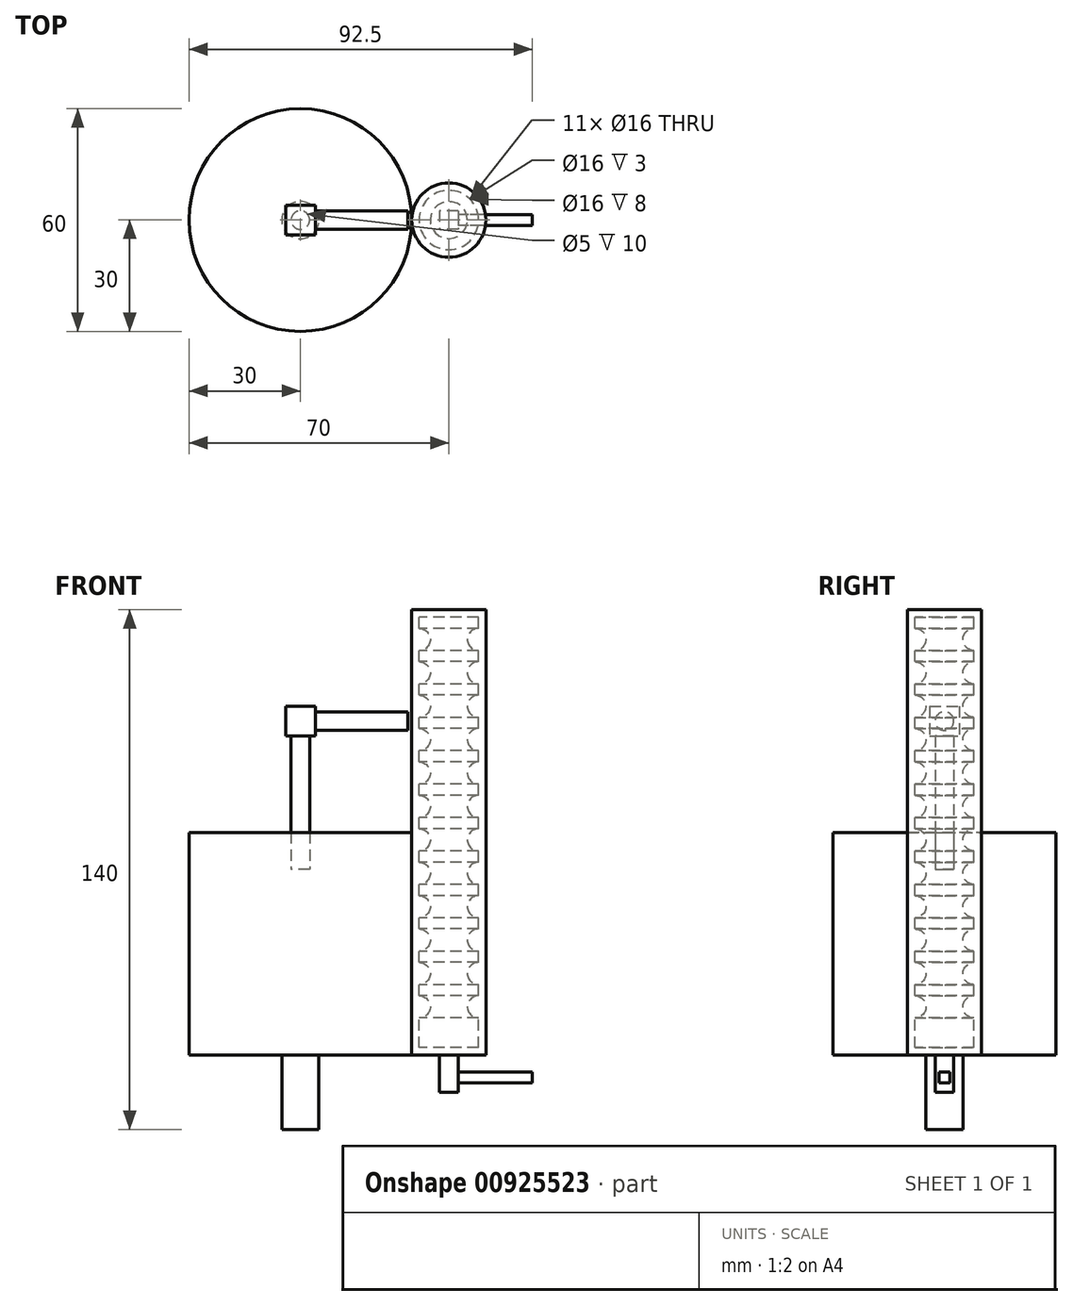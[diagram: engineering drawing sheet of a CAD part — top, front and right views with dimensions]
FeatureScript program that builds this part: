
annotation { "Feature Type Name" : "Feature", "Feature Type Description" : "" }
export const myFeature = defineFeature(function(context is Context, id is Id, definition is map)
    precondition{}
    {
        {
            var Q0;
            Q0=qCreatedBy(makeId("Top.planeOp"),FACE);
            var sketch = newSketch(context, id + "F0", { "sketchPlane" : qUnion([Q0])});
            skCircle(sketch, "E0", {"center": v(0, 0) * mm, "radius": 30 * mm});
            skSolve(sketch);
        }
        {
            var Q0;
            Q0=makeQuery(id+"F0.imprint","IMPRINT",FACE,{"disambiguationData":[TD([[makeQuery(id+"F0.imprint","IMPRINT",EDGE,{"derivedFrom":sQuery(id+"F0.wireOp",EDGE,"E0")}),1.0]])]});
            extrude(context, id + "F1", {"entities" : qUnion([Q0]), "depth" : 60 * mm, "offsetDistance" : 25 * mm});
        }
        {
            var Q0;
            Q0=qCreatedBy(makeId("Front.planeOp"),FACE);
            var sketch = newSketch(context, id + "F2", { "sketchPlane" : qUnion([Q0])});
            skLineSegment(sketch, "E1", {"start": v(40, 0) * mm, "end": v(40, 120) * mm, "construction": true});
            skLineSegment(sketch, "E2", {"start": v(40, 0) * mm, "end": v(40, 120) * mm});
            skLineSegment(sketch, "E3", {"start": v(50, 0) * mm, "end": v(50, 120) * mm});
            skLineSegment(sketch, "E4", {"start": v(50, 120) * mm, "end": v(40, 120) * mm});
            skLineSegment(sketch, "E5", {"start": v(40, 0) * mm, "end": v(50, 0) * mm});
            skSolve(sketch);
        }
        {
            var Q0;
            Q0 = qSketchRegion(id + "F2", true);
            var Q1;
            Q1=sQuery(id+"F2.wireOp",EDGE,"E2");
            revolve(context, id + "F3", {"surfaceOperationType" : NewSurfaceOperationType.NEW, "entities" : qUnion([Q0]), "axis" : qUnion([Q1]), "revolveType" : RevolveType.FULL});
        }
        {
            var Q0;
            Q0=qCreatedBy(makeId("Front.planeOp"),FACE);
            var sketch = newSketch(context, id + "F4", { "sketchPlane" : qUnion([Q0])});
            skLineSegment(sketch, "E6.bottom", {"start": v(40, 2) * mm, "end": v(48, 2) * mm});
            skLineSegment(sketch, "E6.top", {"start": v(40, 118) * mm, "end": v(48, 118) * mm});
            skLineSegment(sketch, "E6.left", {"start": v(40, 2) * mm, "end": v(40, 118) * mm});
            skLineSegment(sketch, "E6.right", {"start": v(48, 2) * mm, "end": v(48, 10) * mm});
            skArc(sketch, "E7", {"start": v(48, 115) * mm, "mid": v(45, 112) * mm, "end": v(48, 109) * mm});
            skArc(sketch, "E8.1.0.0", {"start": v(48, 106) * mm, "mid": v(45, 103) * mm, "end": v(48, 100) * mm});
            skArc(sketch, "E8.2.0.0", {"start": v(48, 97) * mm, "mid": v(45, 94) * mm, "end": v(48, 91) * mm});
            skLineSegment(sketch, "E8.direction1", {"start": v(48, 109) * mm, "end": v(48, 106) * mm, "construction": true});
            skArc(sketch, "E9.0.3.0", {"start": v(48, 88) * mm, "mid": v(45, 85) * mm, "end": v(48, 82) * mm});
            skArc(sketch, "E9.0.4.0", {"start": v(48, 79) * mm, "mid": v(45, 76) * mm, "end": v(48, 73) * mm});
            skArc(sketch, "E9.0.5.0", {"start": v(48, 70) * mm, "mid": v(45, 67) * mm, "end": v(48, 64) * mm});
            skArc(sketch, "E9.0.6.0", {"start": v(48, 61) * mm, "mid": v(45, 58) * mm, "end": v(48, 55) * mm});
            skArc(sketch, "E9.0.7.0", {"start": v(48, 52) * mm, "mid": v(45, 49) * mm, "end": v(48, 46) * mm});
            skArc(sketch, "E9.0.8.0", {"start": v(48, 43) * mm, "mid": v(45, 40) * mm, "end": v(48, 37) * mm});
            skArc(sketch, "E9.0.9.0", {"start": v(48, 34) * mm, "mid": v(45, 31) * mm, "end": v(48, 28) * mm});
            skArc(sketch, "E9.0.10.0", {"start": v(48, 25) * mm, "mid": v(45, 22) * mm, "end": v(48, 19) * mm});
            skArc(sketch, "E9.0.11.0", {"start": v(48, 16) * mm, "mid": v(45, 13) * mm, "end": v(48, 10) * mm});
            skLineSegment(sketch, "E10.trimOffspring", {"start": v(48, 115) * mm, "end": v(48, 118) * mm});
            skLineSegment(sketch, "E11.trimOffspring", {"start": v(48, 106) * mm, "end": v(48, 109) * mm});
            skLineSegment(sketch, "E12.trimOffspring", {"start": v(48, 97) * mm, "end": v(48, 100) * mm});
            skLineSegment(sketch, "E13.trimOffspring", {"start": v(48, 88) * mm, "end": v(48, 91) * mm});
            skLineSegment(sketch, "E14.trimOffspring", {"start": v(48, 79) * mm, "end": v(48, 82) * mm});
            skLineSegment(sketch, "E15.trimOffspring", {"start": v(48, 70) * mm, "end": v(48, 73) * mm});
            skLineSegment(sketch, "E16.trimOffspring", {"start": v(48, 61) * mm, "end": v(48, 64) * mm});
            skLineSegment(sketch, "E17.trimOffspring", {"start": v(48, 52) * mm, "end": v(48, 55) * mm});
            skLineSegment(sketch, "E18.trimOffspring", {"start": v(48, 43) * mm, "end": v(48, 46) * mm});
            skLineSegment(sketch, "E19.trimOffspring", {"start": v(48, 34) * mm, "end": v(48, 37) * mm});
            skLineSegment(sketch, "E20.trimOffspring", {"start": v(48, 25) * mm, "end": v(48, 28) * mm});
            skLineSegment(sketch, "E21.trimOffspring", {"start": v(48, 16) * mm, "end": v(48, 19) * mm});
            skSolve(sketch);
        }
        {
            var Q0;
            Q0 = qSketchRegion(id + "F4", true);
            var Q1;
            Q1=sQuery(id+"F4.wireOp",EDGE,"E6.left");
            revolve(context, id + "F5", {"operationType" : NewBodyOperationType.REMOVE, "surfaceOperationType" : NewSurfaceOperationType.NEW, "entities" : qUnion([Q0]), "axis" : qUnion([Q1]), "revolveType" : RevolveType.FULL, "oppositeDirection" : true});
        }
        {
            var Q0;
            Q0=makeQuery(id+"F1.opExtrude","CAP_FACE",FACE,{"disambiguationData":[OSD([sQuery(id+"F0.wireOp",EDGE,"E0")])],"isStart":true});
            var sketch = newSketch(context, id + "F6", { "sketchPlane" : qUnion([Q0])});
            skCircle(sketch, "E22", {"center": v(0, 0) * mm, "radius": 5 * mm});
            skSolve(sketch);
        }
        {
            var Q0;
            Q0 = qSketchRegion(id + "F6", true);
            extrude(context, id + "F7", {"entities" : qUnion([Q0]), "operationType" : NewBodyOperationType.ADD, "depth" : 20 * mm, "offsetDistance" : 25 * mm});
        }
        {
            var Q0;
            Q0=makeQuery(id+"F3.opRevolve","SWEPT_FACE",FACE,{"disambiguationData":[OSD([sQuery(id+"F2.wireOp",EDGE,"E5")])]});
            var sketch = newSketch(context, id + "F8", { "sketchPlane" : qUnion([Q0])});
            skLineSegment(sketch, "E23.bottom", {"start": v(42.5, -2.5) * mm, "end": v(37.5, -2.5) * mm});
            skLineSegment(sketch, "E23.top", {"start": v(42.5, 2.5) * mm, "end": v(37.5, 2.5) * mm});
            skLineSegment(sketch, "E23.left", {"start": v(42.5, -2.5) * mm, "end": v(42.5, 2.5) * mm});
            skLineSegment(sketch, "E23.right", {"start": v(37.5, -2.5) * mm, "end": v(37.5, 2.5) * mm});
            skPoint(sketch, "E23.middle", {"position": v(40, 0) * mm});
            skSolve(sketch);
        }
        {
            var Q0;
            Q0 = qSketchRegion(id + "F8", true);
            extrude(context, id + "F9", {"entities" : qUnion([Q0]), "operationType" : NewBodyOperationType.ADD, "depth" : 10 * mm, "offsetDistance" : 25 * mm});
        }
        {
            var Q0;
            Q0=makeQuery(id+"F9.opExtrude","SWEPT_FACE",FACE,{"disambiguationData":[OSD([sQuery(id+"F8.wireOp",EDGE,"E23.left")])]});
            var sketch = newSketch(context, id + "F10", { "sketchPlane" : qUnion([Q0])});
            skLineSegment(sketch, "E24.bottom", {"start": v(1.5, -7.5) * mm, "end": v(-1.5, -7.5) * mm});
            skLineSegment(sketch, "E24.top", {"start": v(1.5, -4.5) * mm, "end": v(-1.5, -4.5) * mm});
            skLineSegment(sketch, "E24.left", {"start": v(1.5, -7.5) * mm, "end": v(1.5, -4.5) * mm});
            skLineSegment(sketch, "E24.right", {"start": v(-1.5, -7.5) * mm, "end": v(-1.5, -4.5) * mm});
            skPoint(sketch, "E24.middle", {"position": v(0, -6) * mm});
            skSolve(sketch);
        }
        {
            var Q0;
            Q0 = qSketchRegion(id + "F10", true);
            extrude(context, id + "F11", {"entities" : qUnion([Q0]), "operationType" : NewBodyOperationType.ADD, "depth" : 20 * mm, "offsetDistance" : 25 * mm});
        }
        {
            var Q0;
            Q0=makeQuery(id+"F1.opExtrude","CAP_FACE",FACE,{"disambiguationData":[OSD([sQuery(id+"F0.wireOp",EDGE,"E0")])],"isStart":false});
            var sketch = newSketch(context, id + "F12", { "sketchPlane" : qUnion([Q0])});
            skCircle(sketch, "E25", {"center": v(0, 0) * mm, "radius": 2.5 * mm});
            skSolve(sketch);
        }
        {
            var Q0;
            Q0 = qSketchRegion(id + "F12", true);
            extrude(context, id + "F13", {"entities" : qUnion([Q0]), "depth" : 30 * mm, "offsetDistance" : 25 * mm, "hasSecondDirection" : true, "secondDirectionOppositeDirection" : true, "secondDirectionDepth" : 10 * mm});
        }
        {
            var Q0;
            Q0=makeQuery(id+"F13.opExtrude","SWEPT_BODY",BODY,{"disambiguationData":[OSD([sQuery(id+"F12.wireOp",EDGE,"E25")])]});
            var Q1;
            Q1=makeQuery(id+"F1.opExtrude","SWEPT_BODY",BODY,{"disambiguationData":[OSD([sQuery(id+"F0.wireOp",EDGE,"E0")])]});
            booleanBodies(context, id + "F14", {"operationType" : BooleanOperationType.SUBTRACTION, "tools" : qUnion([Q0]), "targets" : qUnion([Q1]), "keepTools" : true});
        }
        {
            var Q0;
            Q0=makeQuery(id+"F13.opExtrude","CAP_FACE",FACE,{"disambiguationData":[OSD([sQuery(id+"F12.wireOp",EDGE,"E25")])],"isStart":false});
            var sketch = newSketch(context, id + "F15", { "sketchPlane" : qUnion([Q0])});
            skLineSegment(sketch, "E26.bottom", {"start": v(4, -4) * mm, "end": v(-4, -4) * mm});
            skLineSegment(sketch, "E26.top", {"start": v(4, 4) * mm, "end": v(-4, 4) * mm});
            skLineSegment(sketch, "E26.left", {"start": v(4, -4) * mm, "end": v(4, 4) * mm});
            skLineSegment(sketch, "E26.right", {"start": v(-4, -4) * mm, "end": v(-4, 4) * mm});
            skPoint(sketch, "E26.middle", {"position": v(0, 0) * mm});
            skSolve(sketch);
        }
        {
            var Q0;
            Q0 = qSketchRegion(id + "F15", true);
            extrude(context, id + "F16", {"entities" : qUnion([Q0]), "operationType" : NewBodyOperationType.ADD, "endBound" : BoundingType.SYMMETRIC, "depth" : 8 * mm, "offsetDistance" : 25 * mm});
        }
        {
            var Q0;
            Q0=makeQuery(id+"F16.opExtrude","SWEPT_FACE",FACE,{"disambiguationData":[OSD([sQuery(id+"F15.wireOp",EDGE,"E26.left")])]});
            var sketch = newSketch(context, id + "F17", { "sketchPlane" : qUnion([Q0])});
            skCircle(sketch, "E27", {"center": v(0, 90) * mm, "radius": 2.5 * mm});
            skPoint(sketch, "E27.centerSnap0", {"position": v(4, 90) * mm});
            skSolve(sketch);
        }
        {
            var Q0;
            Q0 = qSketchRegion(id + "F17", true);
            extrude(context, id + "F18", {"entities" : qUnion([Q0]), "operationType" : NewBodyOperationType.ADD, "depth" : 25 * mm, "offsetDistance" : 25 * mm});
        }
    });
